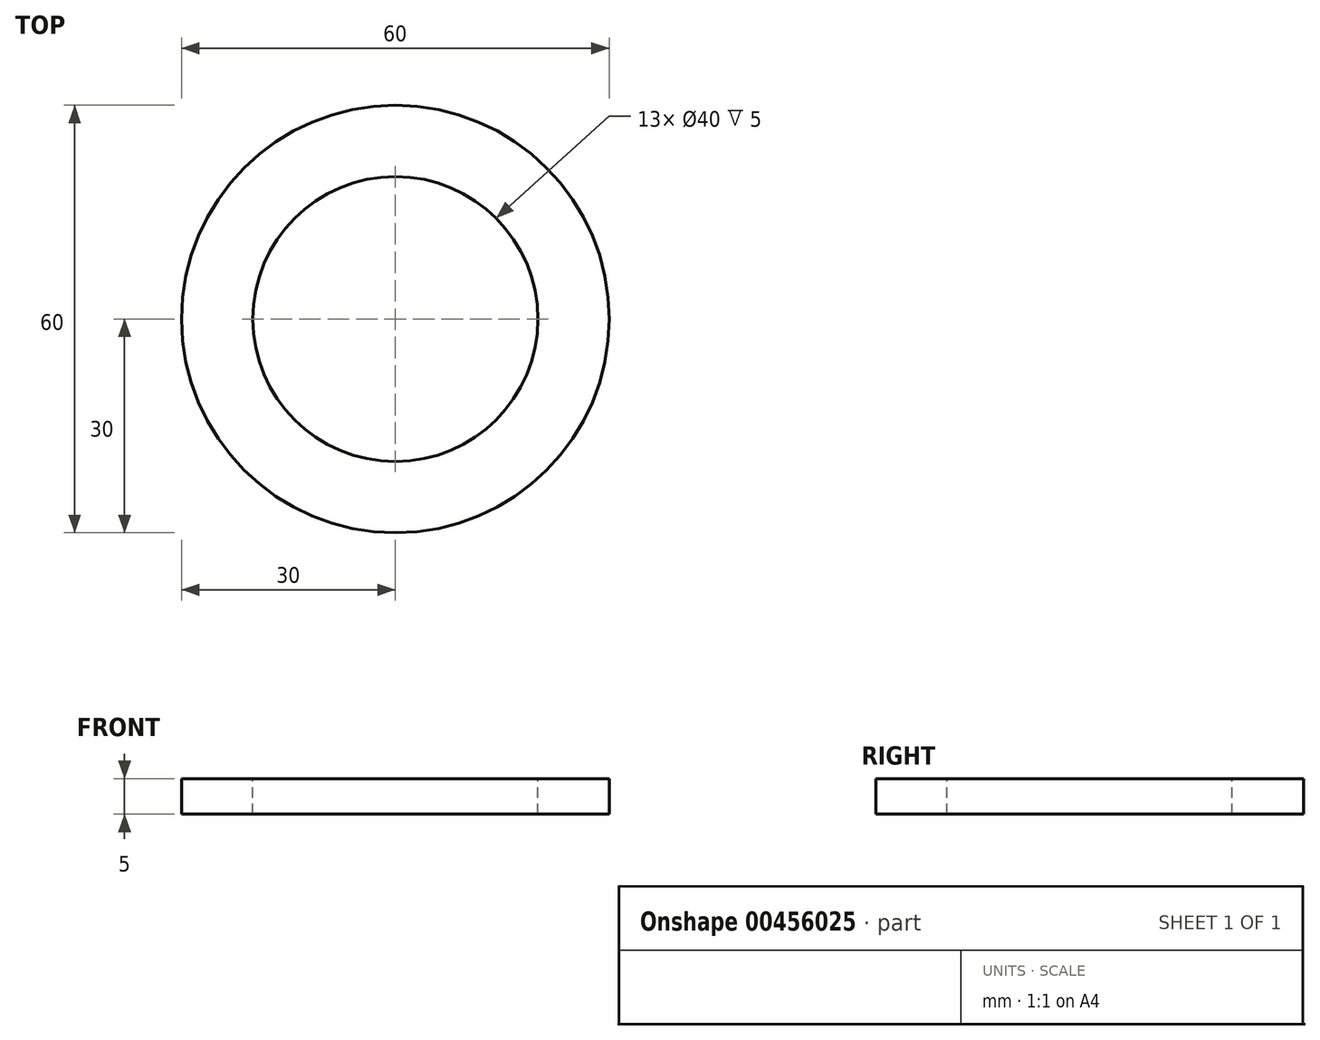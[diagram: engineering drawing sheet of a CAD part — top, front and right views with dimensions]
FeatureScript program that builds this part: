
annotation { "Feature Type Name" : "Feature", "Feature Type Description" : "" }
export const myFeature = defineFeature(function(context is Context, id is Id, definition is map)
    precondition{}
    {
        {
            var Q0;
            Q0=qCreatedBy(makeId("Front.planeOp"),FACE);
            var sketch = newSketch(context, id + "F0", { "sketchPlane" : qUnion([Q0])});
            skLineSegment(sketch, "E0", {"start": v(0, 25.4) * mm, "end": v(0, -21.95) * mm, "construction": true});
            skLineSegment(sketch, "E1.bottom", {"start": v(-30, 0) * mm, "end": v(-20, 0) * mm});
            skLineSegment(sketch, "E1.top", {"start": v(-30, 5) * mm, "end": v(-20, 5) * mm});
            skLineSegment(sketch, "E1.left", {"start": v(-30, 0) * mm, "end": v(-30, 5) * mm});
            skLineSegment(sketch, "E1.right", {"start": v(-20, 0) * mm, "end": v(-20, 5) * mm});
            skSolve(sketch);
        }
        {
            var Q0;
            Q0 = qSketchRegion(id + "F0", true);
            var Q1;
            Q1=sQuery(id+"F0.wireOp",EDGE,"E0");
            revolve(context, id + "F1", {"entities" : qUnion([Q0]), "axis" : qUnion([Q1]), "revolveType" : RevolveType.FULL});
        }
    });
